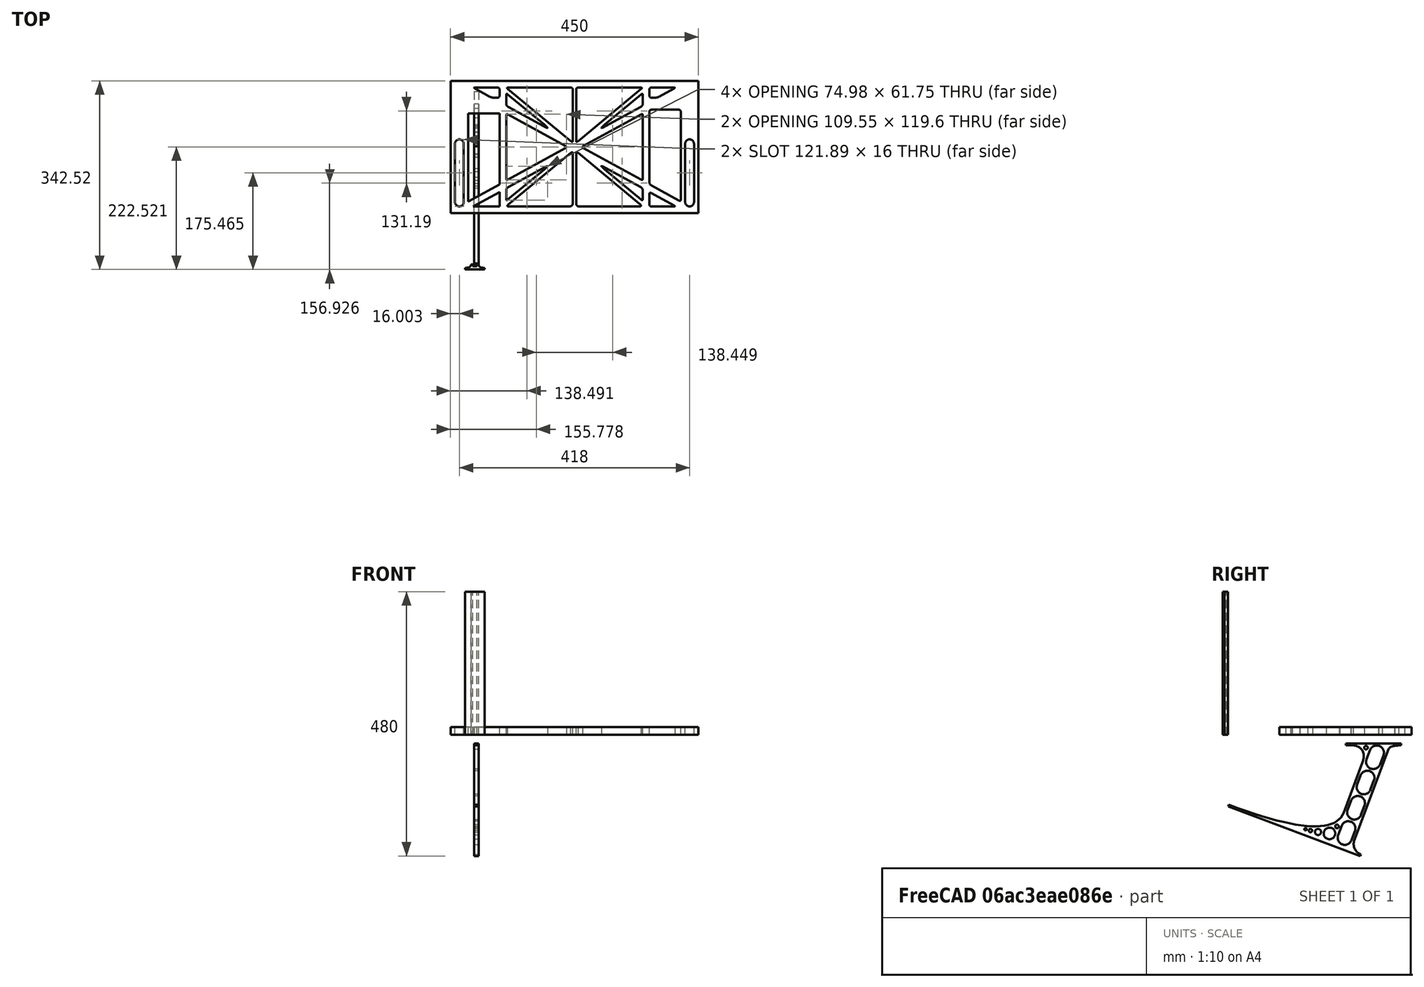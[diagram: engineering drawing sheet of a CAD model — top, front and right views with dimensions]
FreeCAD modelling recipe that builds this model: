
FCSTD DOCUMENT  (FreeCAD 0.19R0.19.2)
Label: laptopStand119FCStd
License: All rights reserved
LicenseURL: http://en.wikipedia.org/wiki/All_rights_reserved
objects: Sketcher::SketchObject×3, Part::Extrusion×3
note: 6 computed .brp shape members not serialized (recipe doc carries the construction recipe); baked Part::Feature solids carry a one-line shape summary decoded from their .brp

FEATURE [Sketcher::SketchObject] Sketch
  FullyConstrained = true
  sketch-geometry (333):
    g0: LineSegment StartX=-10.9272 StartY=-82.7794 StartZ=0 EndX=46.0728 EndY=-51.4823 EndZ=0
    g1: LineSegment StartX=-10.9272 StartY=77.3346 StartZ=0 EndX=-10.9272 EndY=-82.7794 EndZ=0
    g2: LineSegment StartX=-1.92719 StartY=-91.7794 StartZ=0 EndX=46.0728 EndY=-91.7794 EndZ=0
    g3: LineSegment StartX=46.0728 StartY=-65.424 StartZ=0 EndX=-1.92719 EndY=-91.7794 EndZ=0
    g4: LineSegment StartX=46.0728 StartY=-65.424 StartZ=0 EndX=46.0728 EndY=-91.7794 EndZ=0
    g5: LineSegment StartX=46.0728 StartY=77.3346 StartZ=0 EndX=46.0728 EndY=-51.4823 EndZ=0
    g6: LineSegment StartX=-42.9272 StartY=136.221 StartZ=0 EndX=-42.9272 EndY=-103.779 EndZ=0
    g7: LineSegment StartX=407.073 StartY=136.221 StartZ=0 EndX=407.073 EndY=-103.779 EndZ=0
    g8: ArcOfCircle CenterX=-26.9272 CenterY=22.1087 CenterZ=0 NormalX=0 NormalY=0 NormalZ=1 AngleXU=0 Radius=8 StartAngle=1e-16 EndAngle=3.14159
    g9: ArcOfCircle CenterX=-26.9272 CenterY=-83.7794 CenterZ=0 NormalX=0 NormalY=0 NormalZ=1 AngleXU=0 Radius=8 StartAngle=3.14159 EndAngle=6.28319
    g10: LineSegment StartX=-34.9272 StartY=22.1087 StartZ=0 EndX=-34.9272 EndY=-83.7794 EndZ=0
    g11: LineSegment StartX=-18.9272 StartY=22.1087 StartZ=0 EndX=-18.9272 EndY=-83.7794 EndZ=0
    g12: ArcOfCircle CenterX=391.073 CenterY=22.1087 CenterZ=0 NormalX=0 NormalY=0 NormalZ=1 AngleXU=0 Radius=8 StartAngle=-4.4e-15 EndAngle=3.14159
    g13: LineSegment StartX=399.073 StartY=22.1087 StartZ=0 EndX=399.073 EndY=-83.7794 EndZ=0
    g14: LineSegment StartX=383.073 StartY=22.1087 StartZ=0 EndX=383.073 EndY=-83.7794 EndZ=0
    g15: ArcOfCircle CenterX=391.073 CenterY=-83.7794 CenterZ=0 NormalX=0 NormalY=0 NormalZ=1 AngleXU=0 Radius=8 StartAngle=3.14159 EndAngle=6.28319
    g16: Circle CenterX=175.022 CenterY=27.0628 CenterZ=0 NormalX=0 NormalY=0 NormalZ=1 AngleXU=0 Radius=1
    g17: Circle CenterX=179.022 CenterY=24.8665 CenterZ=0 NormalX=0 NormalY=0 NormalZ=1 AngleXU=0 Radius=1
    g18: Circle CenterX=179.022 CenterY=27.0628 CenterZ=0 NormalX=0 NormalY=0 NormalZ=1 AngleXU=0 Radius=1
    g19: BSplineCurve PolesCount=3 KnotsCount=2 Degree=2 IsPeriodic=0
    g20: GeomPoint X=175.022 Y=27.0628 Z=0
    g21: GeomPoint X=179.022 Y=27.0628 Z=0
    g22: Circle CenterX=189.124 CenterY=27.0628 CenterZ=0 NormalX=0 NormalY=0 NormalZ=1 AngleXU=0 Radius=1
    g23: Circle CenterX=185.124 CenterY=24.8665 CenterZ=0 NormalX=0 NormalY=0 NormalZ=1 AngleXU=0 Radius=1
    g24: Circle CenterX=185.124 CenterY=27.0628 CenterZ=0 NormalX=0 NormalY=0 NormalZ=1 AngleXU=0 Radius=1
    g25: BSplineCurve PolesCount=3 KnotsCount=2 Degree=2 IsPeriodic=0
    g26: GeomPoint X=189.124 Y=27.0628 Z=0
    g27: GeomPoint X=185.124 Y=27.0628 Z=0
    g28: Circle CenterX=175.022 CenterY=5.37834 CenterZ=0 NormalX=0 NormalY=0 NormalZ=1 AngleXU=0 Radius=1
    g29: Circle CenterX=179.022 CenterY=7.57463 CenterZ=0 NormalX=0 NormalY=0 NormalZ=1 AngleXU=0 Radius=1
    g30: Circle CenterX=179.022 CenterY=5.34704 CenterZ=0 NormalX=0 NormalY=0 NormalZ=1 AngleXU=0 Radius=1
    g31: BSplineCurve PolesCount=3 KnotsCount=2 Degree=2 IsPeriodic=0
    g32: GeomPoint X=175.022 Y=5.37834 Z=0
    g33: GeomPoint X=179.022 Y=5.34704 Z=0
    g34: Circle CenterX=189.124 CenterY=5.37834 CenterZ=0 NormalX=0 NormalY=0 NormalZ=1 AngleXU=0 Radius=1
    g35: Circle CenterX=185.124 CenterY=7.57463 CenterZ=0 NormalX=0 NormalY=0 NormalZ=1 AngleXU=0 Radius=1
    g36: Circle CenterX=185.124 CenterY=5.34704 CenterZ=0 NormalX=0 NormalY=0 NormalZ=1 AngleXU=0 Radius=1
    g37: BSplineCurve PolesCount=3 KnotsCount=2 Degree=2 IsPeriodic=0
    g38: GeomPoint X=189.124 Y=5.37834 Z=0
    g39: GeomPoint X=185.124 Y=5.34704 Z=0
    g40: Circle CenterX=165.871 CenterY=18.1458 CenterZ=0 NormalX=0 NormalY=0 NormalZ=1 AngleXU=0 Radius=1
    g41: Circle CenterX=169.377 CenterY=16.2206 CenterZ=0 NormalX=0 NormalY=0 NormalZ=1 AngleXU=0 Radius=1
    g42: Circle CenterX=165.871 CenterY=14.2954 CenterZ=0 NormalX=0 NormalY=0 NormalZ=1 AngleXU=0 Radius=1
    g43: BSplineCurve PolesCount=3 KnotsCount=2 Degree=2 IsPeriodic=0
    g44: GeomPoint X=165.871 Y=18.1458 Z=0
    g45: GeomPoint X=165.871 Y=14.2954 Z=0
    g46: Circle CenterX=198.275 CenterY=18.1458 CenterZ=0 NormalX=0 NormalY=0 NormalZ=1 AngleXU=0 Radius=1
    g47: Circle CenterX=194.768 CenterY=16.2206 CenterZ=0 NormalX=0 NormalY=0 NormalZ=1 AngleXU=0 Radius=1
    g48: Circle CenterX=198.275 CenterY=14.2954 CenterZ=0 NormalX=0 NormalY=0 NormalZ=1 AngleXU=0 Radius=1
    g49: BSplineCurve PolesCount=3 KnotsCount=2 Degree=2 IsPeriodic=0
    g50: GeomPoint X=198.275 Y=18.1458 Z=0
    g51: GeomPoint X=198.275 Y=14.2954 Z=0
    g52: LineSegment StartX=407.073 StartY=-103.779 StartZ=0 EndX=-42.9272 EndY=-103.779 EndZ=0
    g53: LineSegment StartX=407.073 StartY=136.221 StartZ=0 EndX=-42.9272 EndY=136.221 EndZ=0
    g54: LineSegment StartX=46.0728 StartY=77.3346 StartZ=0 EndX=-10.9272 EndY=77.3346 EndZ=0
    g55: Circle CenterX=125.607 CenterY=54.1951 CenterZ=0 NormalX=0 NormalY=0 NormalZ=1 AngleXU=0 Radius=1
    g56: Circle CenterX=139.632 CenterY=46.4944 CenterZ=0 NormalX=0 NormalY=0 NormalZ=1 AngleXU=0 Radius=1
    g57: Circle CenterX=127.326 CenterY=56.7187 CenterZ=0 NormalX=0 NormalY=0 NormalZ=1 AngleXU=0 Radius=1
    g58: BSplineCurve PolesCount=3 KnotsCount=2 Degree=2 IsPeriodic=0
    g59: GeomPoint X=125.607 Y=54.1951 Z=0
    g60: GeomPoint X=127.326 Y=56.7187 Z=0
    g61: Circle CenterX=236.821 CenterY=56.7187 CenterZ=0 NormalX=0 NormalY=0 NormalZ=1 AngleXU=0 Radius=1
    g62: Circle CenterX=224.513 CenterY=46.4944 CenterZ=0 NormalX=0 NormalY=0 NormalZ=1 AngleXU=0 Radius=1
    g63: Circle CenterX=238.538 CenterY=54.1951 CenterZ=0 NormalX=0 NormalY=0 NormalZ=1 AngleXU=0 Radius=1
    g64: BSplineCurve PolesCount=3 KnotsCount=2 Degree=2 IsPeriodic=0
    g65: GeomPoint X=236.821 Y=56.7187 Z=0
    g66: GeomPoint X=238.538 Y=54.1951 Z=0
    g67: Circle CenterX=238.538 CenterY=-21.7539 CenterZ=0 NormalX=0 NormalY=0 NormalZ=1 AngleXU=0 Radius=1
    g68: Circle CenterX=224.513 CenterY=-14.0532 CenterZ=0 NormalX=0 NormalY=0 NormalZ=1 AngleXU=0 Radius=1
    g69: Circle CenterX=236.821 CenterY=-24.2775 CenterZ=0 NormalX=0 NormalY=0 NormalZ=1 AngleXU=0 Radius=1
    g70: BSplineCurve PolesCount=3 KnotsCount=2 Degree=2 IsPeriodic=0
    g71: GeomPoint X=238.538 Y=-21.7539 Z=0
    g72: GeomPoint X=236.821 Y=-24.2775 Z=0
    g73: Circle CenterX=125.607 CenterY=-21.7539 CenterZ=0 NormalX=0 NormalY=0 NormalZ=1 AngleXU=0 Radius=1
    g74: Circle CenterX=139.632 CenterY=-14.0532 CenterZ=0 NormalX=0 NormalY=0 NormalZ=1 AngleXU=0 Radius=1
    g75: Circle CenterX=127.325 CenterY=-24.2775 CenterZ=0 NormalX=0 NormalY=0 NormalZ=1 AngleXU=0 Radius=1
    g76: BSplineCurve PolesCount=3 KnotsCount=2 Degree=2 IsPeriodic=0
    g77: GeomPoint X=125.607 Y=-21.7539 Z=0
    g78: GeomPoint X=127.325 Y=-24.2775 Z=0
    g79: Circle CenterX=302.996 CenterY=111.695 CenterZ=0 NormalX=0 NormalY=0 NormalZ=1 AngleXU=0 Radius=1
    g80: Circle CenterX=306.073 CenterY=114.251 CenterZ=0 NormalX=0 NormalY=0 NormalZ=1 AngleXU=0 Radius=1
    g81: Circle CenterX=306.073 CenterY=110.251 CenterZ=0 NormalX=0 NormalY=0 NormalZ=1 AngleXU=0 Radius=1
    g82: BSplineCurve PolesCount=3 KnotsCount=2 Degree=2 IsPeriodic=0
    g83: GeomPoint X=302.996 Y=111.695 Z=0
    g84: GeomPoint X=306.073 Y=110.251 Z=0
    g85: Circle CenterX=306.073 CenterY=95.2763 CenterZ=0 NormalX=0 NormalY=0 NormalZ=1 AngleXU=0 Radius=1
    g86: Circle CenterX=306.073 CenterY=91.2763 CenterZ=0 NormalX=0 NormalY=0 NormalZ=1 AngleXU=0 Radius=1
    g87: Circle CenterX=302.567 CenterY=89.3511 CenterZ=0 NormalX=0 NormalY=0 NormalZ=1 AngleXU=0 Radius=1
    g88: BSplineCurve PolesCount=3 KnotsCount=2 Degree=2 IsPeriodic=0
    g89: GeomPoint X=306.073 Y=95.2763 Z=0
    g90: GeomPoint X=302.567 Y=89.3511 Z=0
    g91: LineSegment StartX=306.073 StartY=110.251 StartZ=0 EndX=306.073 EndY=95.2763 EndZ=0
    g92: LineSegment StartX=302.996 StartY=111.695 StartZ=0 EndX=236.821 EndY=56.7187 EndZ=0
    g93: LineSegment StartX=238.538 StartY=54.1951 StartZ=0 EndX=302.567 EndY=89.3511 EndZ=0
    g94: Circle CenterX=61.1496 CenterY=111.695 CenterZ=0 NormalX=0 NormalY=0 NormalZ=1 AngleXU=0 Radius=1
    g95: Circle CenterX=58.0728 CenterY=114.251 CenterZ=0 NormalX=0 NormalY=0 NormalZ=1 AngleXU=0 Radius=1
    g96: Circle CenterX=58.0728 CenterY=110.251 CenterZ=0 NormalX=0 NormalY=0 NormalZ=1 AngleXU=0 Radius=1
    g97: BSplineCurve PolesCount=3 KnotsCount=2 Degree=2 IsPeriodic=0
    g98: GeomPoint X=61.1496 Y=111.695 Z=0
    g99: GeomPoint X=58.0728 Y=110.251 Z=0
    g100: Circle CenterX=61.5791 CenterY=89.3511 CenterZ=0 NormalX=0 NormalY=0 NormalZ=1 AngleXU=0 Radius=1
    g101: Circle CenterX=58.0728 CenterY=91.2763 CenterZ=0 NormalX=0 NormalY=0 NormalZ=1 AngleXU=0 Radius=1
    g102: Circle CenterX=58.0728 CenterY=95.2763 CenterZ=0 NormalX=0 NormalY=0 NormalZ=1 AngleXU=0 Radius=1
    g103: BSplineCurve PolesCount=3 KnotsCount=2 Degree=2 IsPeriodic=0
    g104: GeomPoint X=61.5791 Y=89.3511 Z=0
    g105: GeomPoint X=58.0728 Y=95.2763 Z=0
    g106: LineSegment StartX=58.0728 StartY=110.251 StartZ=0 EndX=58.0728 EndY=95.2763 EndZ=0
    g107: LineSegment StartX=61.1496 StartY=111.695 StartZ=0 EndX=127.326 EndY=56.7187 EndZ=0
    g108: LineSegment StartX=125.607 StartY=54.1951 StartZ=0 EndX=61.5791 EndY=89.3511 EndZ=0
    g109: Circle CenterX=61.5791 CenterY=-56.9099 CenterZ=0 NormalX=0 NormalY=0 NormalZ=1 AngleXU=0 Radius=1
    g110: Circle CenterX=58.0728 CenterY=-58.8351 CenterZ=0 NormalX=0 NormalY=0 NormalZ=1 AngleXU=0 Radius=1
    g111: Circle CenterX=58.0728 CenterY=-62.8351 CenterZ=0 NormalX=0 NormalY=0 NormalZ=1 AngleXU=0 Radius=1
    g112: BSplineCurve PolesCount=3 KnotsCount=2 Degree=2 IsPeriodic=0
    g113: GeomPoint X=61.5791 Y=-56.9099 Z=0
    g114: GeomPoint X=58.0728 Y=-62.8351 Z=0
    g115: Circle CenterX=58.0728 CenterY=-77.8102 CenterZ=0 NormalX=0 NormalY=0 NormalZ=1 AngleXU=0 Radius=1
    g116: Circle CenterX=58.0728 CenterY=-81.8102 CenterZ=0 NormalX=0 NormalY=0 NormalZ=1 AngleXU=0 Radius=1
    g117: Circle CenterX=61.1496 CenterY=-79.2541 CenterZ=0 NormalX=0 NormalY=0 NormalZ=1 AngleXU=0 Radius=1
    g118: BSplineCurve PolesCount=3 KnotsCount=2 Degree=2 IsPeriodic=0
    g119: GeomPoint X=58.0728 Y=-77.8102 Z=0
    g120: GeomPoint X=61.1496 Y=-79.2541 Z=0
    g121: LineSegment StartX=58.0728 StartY=-62.8351 StartZ=0 EndX=58.0728 EndY=-77.8102 EndZ=0
    g122: LineSegment StartX=61.1496 StartY=-79.2541 StartZ=0 EndX=127.325 EndY=-24.2775 EndZ=0
    g123: LineSegment StartX=125.607 StartY=-21.7539 StartZ=0 EndX=61.5791 EndY=-56.9099 EndZ=0
    g124: Circle CenterX=302.567 CenterY=-56.9099 CenterZ=0 NormalX=0 NormalY=0 NormalZ=1 AngleXU=0 Radius=1
    g125: Circle CenterX=306.073 CenterY=-58.8351 CenterZ=0 NormalX=0 NormalY=0 NormalZ=1 AngleXU=0 Radius=1
    g126: Circle CenterX=306.073 CenterY=-62.8351 CenterZ=0 NormalX=0 NormalY=0 NormalZ=1 AngleXU=0 Radius=1
    g127: BSplineCurve PolesCount=3 KnotsCount=2 Degree=2 IsPeriodic=0
    g128: GeomPoint X=302.567 Y=-56.9099 Z=0
    g129: GeomPoint X=306.073 Y=-62.8351 Z=0
    g130: Circle CenterX=302.996 CenterY=-79.2541 CenterZ=0 NormalX=0 NormalY=0 NormalZ=1 AngleXU=0 Radius=1
    g131: Circle CenterX=306.073 CenterY=-81.8102 CenterZ=0 NormalX=0 NormalY=0 NormalZ=1 AngleXU=0 Radius=1
    g132: Circle CenterX=306.073 CenterY=-77.8102 CenterZ=0 NormalX=0 NormalY=0 NormalZ=1 AngleXU=0 Radius=1
    g133: BSplineCurve PolesCount=3 KnotsCount=2 Degree=2 IsPeriodic=0
    g134: GeomPoint X=302.996 Y=-79.2541 Z=0
    g135: GeomPoint X=306.073 Y=-77.8102 Z=0
    g136: LineSegment StartX=306.073 StartY=-62.8351 StartZ=0 EndX=306.073 EndY=-77.8102 EndZ=0
    g137: LineSegment StartX=302.996 StartY=-79.2541 StartZ=0 EndX=236.821 EndY=-24.2775 EndZ=0
    g138: LineSegment StartX=238.538 StartY=-21.7539 StartZ=0 EndX=302.567 EndY=-56.9099 EndZ=0
    g139: Circle CenterX=61.6457 CenterY=-88.8112 CenterZ=0 NormalX=0 NormalY=0 NormalZ=1 AngleXU=0 Radius=1
    g140: Circle CenterX=58.0728 CenterY=-91.7794 CenterZ=0 NormalX=0 NormalY=0 NormalZ=1 AngleXU=0 Radius=1
    g141: Circle CenterX=63.9135 CenterY=-91.7794 CenterZ=0 NormalX=0 NormalY=0 NormalZ=1 AngleXU=0 Radius=1
    g142: BSplineCurve PolesCount=3 KnotsCount=2 Degree=2 IsPeriodic=0
    g143: GeomPoint X=61.6457 Y=-88.8112 Z=0
    g144: GeomPoint X=63.9135 Y=-91.7794 Z=0
    g145: Circle CenterX=179.022 CenterY=-85.8163 CenterZ=0 NormalX=0 NormalY=0 NormalZ=1 AngleXU=0 Radius=1
    g146: Circle CenterX=179.022 CenterY=-91.7794 CenterZ=0 NormalX=0 NormalY=0 NormalZ=1 AngleXU=0 Radius=1
    g147: Circle CenterX=171.895 CenterY=-91.7794 CenterZ=0 NormalX=0 NormalY=0 NormalZ=1 AngleXU=0 Radius=1
    g148: BSplineCurve PolesCount=3 KnotsCount=2 Degree=2 IsPeriodic=0
    g149: GeomPoint X=179.022 Y=-85.8163 Z=0
    g150: GeomPoint X=171.895 Y=-91.7794 Z=0
    g151: Circle CenterX=185.124 CenterY=-86.2028 CenterZ=0 NormalX=0 NormalY=0 NormalZ=1 AngleXU=0 Radius=1
    g152: Circle CenterX=185.124 CenterY=-91.7794 CenterZ=0 NormalX=0 NormalY=0 NormalZ=1 AngleXU=0 Radius=1
    g153: Circle CenterX=191.747 CenterY=-91.7794 CenterZ=0 NormalX=0 NormalY=0 NormalZ=1 AngleXU=0 Radius=1
    g154: BSplineCurve PolesCount=3 KnotsCount=2 Degree=2 IsPeriodic=0
    g155: GeomPoint X=185.124 Y=-86.2028 Z=0
    g156: GeomPoint X=191.747 Y=-91.7794 Z=0
    g157: Circle CenterX=299.888 CenterY=-86.6413 CenterZ=0 NormalX=0 NormalY=0 NormalZ=1 AngleXU=0 Radius=1
    g158: Circle CenterX=306.073 CenterY=-91.7794 CenterZ=0 NormalX=0 NormalY=0 NormalZ=1 AngleXU=0 Radius=1
    g159: Circle CenterX=298.776 CenterY=-91.7794 CenterZ=0 NormalX=0 NormalY=0 NormalZ=1 AngleXU=0 Radius=1
    g160: BSplineCurve PolesCount=3 KnotsCount=2 Degree=2 IsPeriodic=0
    g161: GeomPoint X=299.888 Y=-86.6413 Z=0
    g162: GeomPoint X=298.776 Y=-91.7794 Z=0
    g163: LineSegment StartX=189.124 StartY=5.37834 StartZ=0 EndX=299.888 EndY=-86.6413 EndZ=0
    g164: LineSegment StartX=298.776 StartY=-91.7794 StartZ=0 EndX=191.747 EndY=-91.7794 EndZ=0
    g165: LineSegment StartX=185.124 StartY=-86.2028 StartZ=0 EndX=185.124 EndY=5.34704 EndZ=0
    g166: LineSegment StartX=179.022 StartY=5.34704 StartZ=0 EndX=179.022 EndY=-85.8163 EndZ=0
    g167: LineSegment StartX=171.895 StartY=-91.7794 StartZ=0 EndX=63.9135 EndY=-91.7794 EndZ=0
    g168: LineSegment StartX=61.6457 StartY=-88.8112 StartZ=0 EndX=175.022 EndY=5.37834 EndZ=0
    g169: Circle CenterX=302.073 CenterY=124.221 CenterZ=0 NormalX=0 NormalY=0 NormalZ=1 AngleXU=0 Radius=1
    g170: Circle CenterX=306.073 CenterY=124.221 CenterZ=0 NormalX=0 NormalY=0 NormalZ=1 AngleXU=0 Radius=1
    g171: Circle CenterX=302.996 CenterY=121.665 CenterZ=0 NormalX=0 NormalY=0 NormalZ=1 AngleXU=0 Radius=1
    g172: BSplineCurve PolesCount=3 KnotsCount=2 Degree=2 IsPeriodic=0
    g173: GeomPoint X=302.073 Y=124.221 Z=0
    g174: GeomPoint X=302.996 Y=121.665 Z=0
    g175: Circle CenterX=189.124 CenterY=124.221 CenterZ=0 NormalX=0 NormalY=0 NormalZ=1 AngleXU=0 Radius=1
    g176: Circle CenterX=185.124 CenterY=124.221 CenterZ=0 NormalX=0 NormalY=0 NormalZ=1 AngleXU=0 Radius=1
    g177: Circle CenterX=185.124 CenterY=120.221 CenterZ=0 NormalX=0 NormalY=0 NormalZ=1 AngleXU=0 Radius=1
    g178: BSplineCurve PolesCount=3 KnotsCount=2 Degree=2 IsPeriodic=0
    g179: GeomPoint X=189.124 Y=124.221 Z=0
    g180: GeomPoint X=185.124 Y=120.221 Z=0
    g181: Circle CenterX=175.022 CenterY=124.221 CenterZ=0 NormalX=0 NormalY=0 NormalZ=1 AngleXU=0 Radius=1
    g182: Circle CenterX=179.022 CenterY=124.221 CenterZ=0 NormalX=0 NormalY=0 NormalZ=1 AngleXU=0 Radius=1
    g183: Circle CenterX=179.022 CenterY=120.221 CenterZ=0 NormalX=0 NormalY=0 NormalZ=1 AngleXU=0 Radius=1
    g184: BSplineCurve PolesCount=3 KnotsCount=2 Degree=2 IsPeriodic=0
    g185: GeomPoint X=175.022 Y=124.221 Z=0
    g186: GeomPoint X=179.022 Y=120.221 Z=0
    g187: Circle CenterX=62.0728 CenterY=124.221 CenterZ=0 NormalX=0 NormalY=0 NormalZ=1 AngleXU=0 Radius=1
    g188: Circle CenterX=58.0728 CenterY=124.221 CenterZ=0 NormalX=0 NormalY=0 NormalZ=1 AngleXU=0 Radius=1
    g189: Circle CenterX=61.1496 CenterY=121.665 CenterZ=0 NormalX=0 NormalY=0 NormalZ=1 AngleXU=0 Radius=1
    g190: BSplineCurve PolesCount=3 KnotsCount=2 Degree=2 IsPeriodic=0
    g191: GeomPoint X=62.0728 Y=124.221 Z=0
    g192: GeomPoint X=61.1496 Y=121.665 Z=0
    g193: LineSegment StartX=62.0728 StartY=124.221 StartZ=0 EndX=175.022 EndY=124.221 EndZ=0
    g194: LineSegment StartX=179.022 StartY=120.221 StartZ=0 EndX=179.022 EndY=27.0628 EndZ=0
    g195: LineSegment StartX=185.124 StartY=27.0628 StartZ=0 EndX=185.124 EndY=120.221 EndZ=0
    g196: LineSegment StartX=189.124 StartY=124.221 StartZ=0 EndX=302.073 EndY=124.221 EndZ=0
    g197: LineSegment StartX=302.996 StartY=121.665 StartZ=0 EndX=189.124 EndY=27.0628 EndZ=0
    g198: LineSegment StartX=175.022 StartY=27.0628 StartZ=0 EndX=61.1496 EndY=121.665 EndZ=0
    g199: Circle CenterX=61.5791 CenterY=75.4095 CenterZ=0 NormalX=0 NormalY=0 NormalZ=1 AngleXU=0 Radius=1
    g200: Circle CenterX=58.0728 CenterY=77.3346 CenterZ=0 NormalX=0 NormalY=0 NormalZ=1 AngleXU=0 Radius=1
    g201: Circle CenterX=58.0728 CenterY=73.3346 CenterZ=0 NormalX=0 NormalY=0 NormalZ=1 AngleXU=0 Radius=1
    g202: BSplineCurve PolesCount=3 KnotsCount=2 Degree=2 IsPeriodic=0
    g203: GeomPoint X=61.5791 Y=75.4095 Z=0
    g204: GeomPoint X=58.0728 Y=73.3346 Z=0
    g205: Circle CenterX=58.0728 CenterY=-40.8935 CenterZ=0 NormalX=0 NormalY=0 NormalZ=1 AngleXU=0 Radius=1
    g206: Circle CenterX=58.0728 CenterY=-44.8935 CenterZ=0 NormalX=0 NormalY=0 NormalZ=1 AngleXU=0 Radius=1
    g207: Circle CenterX=61.5791 CenterY=-42.9683 CenterZ=0 NormalX=0 NormalY=0 NormalZ=1 AngleXU=0 Radius=1
    g208: BSplineCurve PolesCount=3 KnotsCount=2 Degree=2 IsPeriodic=0
    g209: GeomPoint X=58.0728 Y=-40.8935 Z=0
    g210: GeomPoint X=61.5791 Y=-42.9683 Z=0
    g211: LineSegment StartX=61.5791 StartY=-42.9683 StartZ=0 EndX=165.871 EndY=14.2954 EndZ=0
    g212: LineSegment StartX=165.871 StartY=18.1458 StartZ=0 EndX=61.5791 EndY=75.4095 EndZ=0
    g213: LineSegment StartX=58.0728 StartY=73.3346 StartZ=0 EndX=58.0728 EndY=-40.8935 EndZ=0
    g214: Circle CenterX=302.567 CenterY=-42.9683 CenterZ=0 NormalX=0 NormalY=0 NormalZ=1 AngleXU=0 Radius=1
    g215: Circle CenterX=306.073 CenterY=-44.8935 CenterZ=0 NormalX=0 NormalY=0 NormalZ=1 AngleXU=0 Radius=1
    g216: Circle CenterX=306.073 CenterY=-40.8935 CenterZ=0 NormalX=0 NormalY=0 NormalZ=1 AngleXU=0 Radius=1
    g217: BSplineCurve PolesCount=3 KnotsCount=2 Degree=2 IsPeriodic=0
    g218: GeomPoint X=302.567 Y=-42.9683 Z=0
    g219: GeomPoint X=306.073 Y=-40.8935 Z=0
    g220: Circle CenterX=306.073 CenterY=73.3346 CenterZ=0 NormalX=0 NormalY=0 NormalZ=1 AngleXU=0 Radius=1
    g221: Circle CenterX=306.073 CenterY=77.3346 CenterZ=0 NormalX=0 NormalY=0 NormalZ=1 AngleXU=0 Radius=1
    g222: Circle CenterX=302.567 CenterY=75.4095 CenterZ=0 NormalX=0 NormalY=0 NormalZ=1 AngleXU=0 Radius=1
    g223: BSplineCurve PolesCount=3 KnotsCount=2 Degree=2 IsPeriodic=0
    g224: GeomPoint X=306.073 Y=73.3346 Z=0
    g225: GeomPoint X=302.567 Y=75.4095 Z=0
    g226: LineSegment StartX=302.567 StartY=-42.9683 StartZ=0 EndX=198.275 EndY=14.2954 EndZ=0
    g227: LineSegment StartX=198.275 StartY=18.1458 StartZ=0 EndX=302.567 EndY=75.4095 EndZ=0
    g228: LineSegment StartX=306.073 StartY=73.3346 StartZ=0 EndX=306.073 EndY=-40.8935 EndZ=0
    g229: LineSegment StartX=322.073 StartY=105.865 StartZ=0 EndX=328.643 EndY=105.865 EndZ=0
    g230: LineSegment StartX=318.073 StartY=120.221 StartZ=0 EndX=318.073 EndY=109.865 EndZ=0
    g231: LineSegment StartX=336.157 StartY=107.779 StartZ=0 EndX=362.567 EndY=122.294 EndZ=0
    g232: Circle CenterX=362.073 CenterY=124.221 CenterZ=0 NormalX=0 NormalY=0 NormalZ=1 AngleXU=0 Radius=1
    g233: Circle CenterX=366.073 CenterY=124.221 CenterZ=0 NormalX=0 NormalY=0 NormalZ=1 AngleXU=0 Radius=1
    g234: Circle CenterX=362.567 CenterY=122.294 CenterZ=0 NormalX=0 NormalY=0 NormalZ=1 AngleXU=0 Radius=1
    g235: BSplineCurve PolesCount=3 KnotsCount=2 Degree=2 IsPeriodic=0
    g236: GeomPoint X=362.073 Y=124.221 Z=0
    g237: GeomPoint X=362.567 Y=122.294 Z=0
    g238: Circle CenterX=322.073 CenterY=124.221 CenterZ=0 NormalX=0 NormalY=0 NormalZ=1 AngleXU=0 Radius=1
    g239: Circle CenterX=318.073 CenterY=124.221 CenterZ=0 NormalX=0 NormalY=0 NormalZ=1 AngleXU=0 Radius=1
    g240: Circle CenterX=318.073 CenterY=120.221 CenterZ=0 NormalX=0 NormalY=0 NormalZ=1 AngleXU=0 Radius=1
    g241: BSplineCurve PolesCount=3 KnotsCount=2 Degree=2 IsPeriodic=0
    g242: GeomPoint X=322.073 Y=124.221 Z=0
    g243: GeomPoint X=318.073 Y=120.221 Z=0
    g244: Circle CenterX=322.073 CenterY=105.865 CenterZ=0 NormalX=0 NormalY=0 NormalZ=1 AngleXU=0 Radius=1
    g245: Circle CenterX=318.073 CenterY=105.865 CenterZ=0 NormalX=0 NormalY=0 NormalZ=1 AngleXU=0 Radius=1
    g246: Circle CenterX=318.073 CenterY=109.865 CenterZ=0 NormalX=0 NormalY=0 NormalZ=1 AngleXU=0 Radius=1
    g247: BSplineCurve PolesCount=3 KnotsCount=2 Degree=2 IsPeriodic=0
    g248: GeomPoint X=322.073 Y=105.865 Z=0
    g249: GeomPoint X=318.073 Y=109.865 Z=0
    g250: Circle CenterX=336.157 CenterY=107.779 CenterZ=0 NormalX=0 NormalY=0 NormalZ=1 AngleXU=0 Radius=1
    g251: Circle CenterX=332.651 CenterY=105.853 CenterZ=0 NormalX=0 NormalY=0 NormalZ=1 AngleXU=0 Radius=1
    g252: Circle CenterX=328.643 CenterY=105.865 CenterZ=0 NormalX=0 NormalY=0 NormalZ=1 AngleXU=0 Radius=1
    g253: BSplineCurve PolesCount=3 KnotsCount=2 Degree=2 IsPeriodic=0
    g254: GeomPoint X=336.157 Y=107.779 Z=0
    g255: GeomPoint X=328.643 Y=105.865 Z=0
    g256: LineSegment StartX=322.073 StartY=124.221 StartZ=0 EndX=362.073 EndY=124.221 EndZ=0
    g257: Circle CenterX=371.567 CenterY=-80.8644 CenterZ=0 NormalX=0 NormalY=0 NormalZ=1 AngleXU=0 Radius=1
    g258: Circle CenterX=375.073 CenterY=-82.7896 CenterZ=0 NormalX=0 NormalY=0 NormalZ=1 AngleXU=0 Radius=1
    g259: Circle CenterX=375.073 CenterY=-78.7896 CenterZ=0 NormalX=0 NormalY=0 NormalZ=1 AngleXU=0 Radius=1
    g260: BSplineCurve PolesCount=3 KnotsCount=2 Degree=2 IsPeriodic=0
    g261: GeomPoint X=371.567 Y=-80.8644 Z=0
    g262: GeomPoint X=375.073 Y=-78.7896 Z=0
    g263: Circle CenterX=321.579 CenterY=-53.4075 CenterZ=0 NormalX=0 NormalY=0 NormalZ=1 AngleXU=0 Radius=1
    g264: Circle CenterX=318.073 CenterY=-51.4823 CenterZ=0 NormalX=0 NormalY=0 NormalZ=1 AngleXU=0 Radius=1
    g265: Circle CenterX=318.073 CenterY=-47.4823 CenterZ=0 NormalX=0 NormalY=0 NormalZ=1 AngleXU=0 Radius=1
    g266: BSplineCurve PolesCount=3 KnotsCount=2 Degree=2 IsPeriodic=0
    g267: GeomPoint X=321.579 Y=-53.4075 Z=0
    g268: GeomPoint X=318.073 Y=-47.4823 Z=0
    g269: Circle CenterX=318.073 CenterY=79.9235 CenterZ=0 NormalX=0 NormalY=0 NormalZ=1 AngleXU=0 Radius=1
    g270: Circle CenterX=318.073 CenterY=83.9235 CenterZ=0 NormalX=0 NormalY=0 NormalZ=1 AngleXU=0 Radius=1
    g271: Circle CenterX=322.073 CenterY=83.9235 CenterZ=0 NormalX=0 NormalY=0 NormalZ=1 AngleXU=0 Radius=1
    g272: BSplineCurve PolesCount=3 KnotsCount=2 Degree=2 IsPeriodic=0
    g273: GeomPoint X=318.073 Y=79.9235 Z=0
    g274: GeomPoint X=322.073 Y=83.9235 Z=0
    g275: Circle CenterX=375.073 CenterY=79.9235 CenterZ=0 NormalX=0 NormalY=0 NormalZ=1 AngleXU=0 Radius=1
    g276: Circle CenterX=375.073 CenterY=83.9235 CenterZ=0 NormalX=0 NormalY=0 NormalZ=1 AngleXU=0 Radius=1
    g277: Circle CenterX=371.073 CenterY=83.9235 CenterZ=0 NormalX=0 NormalY=0 NormalZ=1 AngleXU=0 Radius=1
    g278: BSplineCurve PolesCount=3 KnotsCount=2 Degree=2 IsPeriodic=0
    g279: GeomPoint X=375.073 Y=79.9235 Z=0
    g280: GeomPoint X=371.073 Y=83.9235 Z=0
    g281: LineSegment StartX=322.073 StartY=83.9235 StartZ=0 EndX=371.073 EndY=83.9235 EndZ=0
    g282: LineSegment StartX=375.073 StartY=79.9235 StartZ=0 EndX=375.073 EndY=-78.7896 EndZ=0
    g283: LineSegment StartX=371.567 StartY=-80.8644 StartZ=0 EndX=321.579 EndY=-53.4075 EndZ=0
    g284: LineSegment StartX=318.073 StartY=-47.4823 StartZ=0 EndX=318.073 EndY=79.9235 EndZ=0
    g285: Circle CenterX=321.579 CenterY=-67.3492 CenterZ=0 NormalX=0 NormalY=0 NormalZ=1 AngleXU=0 Radius=1
    g286: Circle CenterX=318.073 CenterY=-65.424 CenterZ=0 NormalX=0 NormalY=0 NormalZ=1 AngleXU=0 Radius=1
    g287: Circle CenterX=318.073 CenterY=-69.424 CenterZ=0 NormalX=0 NormalY=0 NormalZ=1 AngleXU=0 Radius=1
    g288: BSplineCurve PolesCount=3 KnotsCount=2 Degree=2 IsPeriodic=0
    g289: GeomPoint X=321.579 Y=-67.3492 Z=0
    g290: GeomPoint X=318.073 Y=-69.424 Z=0
    g291: Circle CenterX=362.567 CenterY=-89.8542 CenterZ=0 NormalX=0 NormalY=0 NormalZ=1 AngleXU=0 Radius=1
    g292: Circle CenterX=366.073 CenterY=-91.7794 CenterZ=0 NormalX=0 NormalY=0 NormalZ=1 AngleXU=0 Radius=1
    g293: Circle CenterX=362.073 CenterY=-91.7794 CenterZ=0 NormalX=0 NormalY=0 NormalZ=1 AngleXU=0 Radius=1
    g294: BSplineCurve PolesCount=3 KnotsCount=2 Degree=2 IsPeriodic=0
    g295: GeomPoint X=362.567 Y=-89.8542 Z=0
    g296: GeomPoint X=362.073 Y=-91.7794 Z=0
    g297: Circle CenterX=322.073 CenterY=-91.7794 CenterZ=0 NormalX=0 NormalY=0 NormalZ=1 AngleXU=0 Radius=1
    g298: Circle CenterX=318.073 CenterY=-91.7794 CenterZ=0 NormalX=0 NormalY=0 NormalZ=1 AngleXU=0 Radius=1
    g299: Circle CenterX=318.073 CenterY=-87.7794 CenterZ=0 NormalX=0 NormalY=0 NormalZ=1 AngleXU=0 Radius=1
    g300: BSplineCurve PolesCount=3 KnotsCount=2 Degree=2 IsPeriodic=0
    g301: GeomPoint X=322.073 Y=-91.7794 Z=0
    g302: GeomPoint X=318.073 Y=-87.7794 Z=0
    g303: LineSegment StartX=362.567 StartY=-89.8542 StartZ=0 EndX=321.579 EndY=-67.3492 EndZ=0
    g304: LineSegment StartX=318.073 StartY=-69.424 StartZ=0 EndX=318.073 EndY=-87.7794 EndZ=0
    g305: LineSegment StartX=322.073 StartY=-91.7794 StartZ=0 EndX=362.073 EndY=-91.7794 EndZ=0
    g306: Circle CenterX=2.07281 CenterY=124.221 CenterZ=0 NormalX=0 NormalY=0 NormalZ=1 AngleXU=0 Radius=1
    g307: Circle CenterX=1.57905 CenterY=122.295 CenterZ=0 NormalX=0 NormalY=0 NormalZ=1 AngleXU=0 Radius=1
    g308: BSplineCurve PolesCount=3 KnotsCount=2 Degree=2 IsPeriodic=0
    g309: GeomPoint X=2.07281 Y=124.221 Z=0
    g310: GeomPoint X=1.57905 Y=122.295 Z=0
    g311: Circle CenterX=42.0728 CenterY=124.221 CenterZ=0 NormalX=0 NormalY=0 NormalZ=1 AngleXU=0 Radius=1
    g312: Circle CenterX=46.0728 CenterY=124.221 CenterZ=0 NormalX=0 NormalY=0 NormalZ=1 AngleXU=0 Radius=1
    g313: Circle CenterX=46.0728 CenterY=120.221 CenterZ=0 NormalX=0 NormalY=0 NormalZ=1 AngleXU=0 Radius=1
    g314: BSplineCurve PolesCount=3 KnotsCount=2 Degree=2 IsPeriodic=0
    g315: GeomPoint X=42.0728 Y=124.221 Z=0
    g316: GeomPoint X=46.0728 Y=120.221 Z=0
    g317: Circle CenterX=46.0728 CenterY=109.865 CenterZ=0 NormalX=0 NormalY=0 NormalZ=1 AngleXU=0 Radius=1
    g318: Circle CenterX=46.0728 CenterY=105.865 CenterZ=0 NormalX=0 NormalY=0 NormalZ=1 AngleXU=0 Radius=1
    g319: Circle CenterX=42.0728 CenterY=105.865 CenterZ=0 NormalX=0 NormalY=0 NormalZ=1 AngleXU=0 Radius=1
    g320: BSplineCurve PolesCount=3 KnotsCount=2 Degree=2 IsPeriodic=0
    g321: GeomPoint X=46.0728 Y=109.865 Z=0
    g322: GeomPoint X=42.0728 Y=105.865 Z=0
    g323: Circle CenterX=35.5028 CenterY=105.865 CenterZ=0 NormalX=0 NormalY=0 NormalZ=1 AngleXU=0 Radius=1
    g324: Circle CenterX=31.5028 CenterY=105.865 CenterZ=0 NormalX=0 NormalY=0 NormalZ=1 AngleXU=0 Radius=1
    g325: Circle CenterX=27.9965 CenterY=107.79 CenterZ=0 NormalX=0 NormalY=0 NormalZ=1 AngleXU=0 Radius=1
    g326: BSplineCurve PolesCount=3 KnotsCount=2 Degree=2 IsPeriodic=0
    g327: GeomPoint X=35.5028 Y=105.865 Z=0
    g328: GeomPoint X=27.9965 Y=107.79 Z=0
    g329: LineSegment StartX=2.07281 StartY=124.221 StartZ=0 EndX=42.0728 EndY=124.221 EndZ=0
    g330: LineSegment StartX=46.0728 StartY=120.221 StartZ=0 EndX=46.0728 EndY=109.865 EndZ=0
    g331: LineSegment StartX=42.0728 StartY=105.865 StartZ=0 EndX=35.5028 EndY=105.865 EndZ=0
    g332: LineSegment StartX=27.9965 StartY=107.79 StartZ=0 EndX=1.57905 EndY=122.295 EndZ=0
  constraints (552):
    c: Horizontal(g2)
    c: Coincident(g4,g3)
    c: Coincident(g0,g5)
    c: Block(g4)
    c: Block(g3)
    c: Block(g0)
    c: Block(g1)
    c: Block(g2)
    c: Vertical(g6)
    c: Vertical(g7)
    c: Block(g7)
    c: Block(g6)
    c: Tangent(g8,g11) = 1.5708
    c: Tangent(g8,g10) = -1.5708
    c: Tangent(g10,g9) = -1.5708
    c: Tangent(g11,g9) = 1.5708
    c: Vertical(g10)
    c: Equal(g8,g9)
    c: Block(g11)
    c: Block(g10)
    c: Tangent(g12,g13) = 1.5708
    c: Tangent(g13,g15) = 1.5708
    c: Equal(g12,g15)
    c: Coincident(g14,g12)
    c: Coincident(g14,g15)
    c: Block(g13)
    c: Block(g14)
    c: Weight(g16) = 1
    c: Equal(g16,g17)
    c: Equal(g16,g18)
    c: InternalAlignment(g16,g19)
    c: InternalAlignment(g17,g19)
    c: InternalAlignment(g18,g19)
    c: InternalAlignment(g20,g19)
    c: InternalAlignment(g21,g19)
    c: Weight(g22) = 1
    c: Equal(g22,g23)
    c: Equal(g22,g24)
    c: InternalAlignment(g22,g25)
    c: InternalAlignment(g23,g25)
    c: InternalAlignment(g24,g25)
    c: InternalAlignment(g26,g25)
    c: InternalAlignment(g27,g25)
    c: Block(g25)
    c: Block(g19)
    c: Weight(g28) = 1
    c: Equal(g28,g29)
    c: Equal(g28,g30)
    c: InternalAlignment(g28,g31)
    c: InternalAlignment(g29,g31)
    c: InternalAlignment(g30,g31)
    c: InternalAlignment(g32,g31)
    c: InternalAlignment(g33,g31)
    c: Weight(g34) = 1
    c: Equal(g34,g35)
    c: Equal(g34,g36)
    c: InternalAlignment(g34,g37)
    c: InternalAlignment(g35,g37)
    c: InternalAlignment(g36,g37)
    c: InternalAlignment(g38,g37)
    c: InternalAlignment(g39,g37)
    c: Block(g37)
    c: Block(g31)
    c: Weight(g40) = 1
    c: Equal(g40,g41)
    c: Equal(g40,g42)
    c: InternalAlignment(g40,g43)
    c: InternalAlignment(g41,g43)
    c: InternalAlignment(g42,g43)
    c: InternalAlignment(g44,g43)
    c: InternalAlignment(g45,g43)
    c: Weight(g46) = 1
    c: Equal(g46,g47)
    c: Equal(g46,g48)
    c: InternalAlignment(g46,g49)
    c: InternalAlignment(g47,g49)
    c: InternalAlignment(g48,g49)
    c: InternalAlignment(g50,g49)
    c: InternalAlignment(g51,g49)
    c: Block(g43)
    c: Block(g49)
    c: Coincident(g52,g7)
    c: Coincident(g52,g6)
    c: Horizontal(g52)
    c: Distance(g52) = 450
    c: Coincident(g53,g7)
    c: Coincident(g53,g6)
    c: Horizontal(g53)
    c: Horizontal(g54)
    c: Coincident(g5,g54)
    c: Block(g54)
    c: Coincident(g1,g54)
    c: Weight(g55) = 1
    c: Equal(g55,g56)
    c: Equal(g55,g57)
    c: InternalAlignment(g55,g58)
    c: InternalAlignment(g56,g58)
    c: InternalAlignment(g57,g58)
    c: InternalAlignment(g59,g58)
    c: InternalAlignment(g60,g58)
    c: Block(g58)
    c: Weight(g61) = 1
    c: Equal(g61,g62)
    c: Equal(g61,g63)
    c: InternalAlignment(g61,g64)
    c: InternalAlignment(g62,g64)
    c: InternalAlignment(g63,g64)
    c: InternalAlignment(g65,g64)
    c: InternalAlignment(g66,g64)
    c: Block(g64)
    c: Weight(g67) = 1
    c: Equal(g67,g68)
    c: Equal(g67,g69)
    c: InternalAlignment(g67,g70)
    c: InternalAlignment(g68,g70)
    c: InternalAlignment(g69,g70)
    c: InternalAlignment(g71,g70)
    c: InternalAlignment(g72,g70)
    c: Block(g70)
    c: Weight(g73) = 1
    c: Equal(g73,g74)
    c: Equal(g73,g75)
    c: InternalAlignment(g73,g76)
    c: InternalAlignment(g74,g76)
    c: InternalAlignment(g75,g76)
    c: InternalAlignment(g77,g76)
    c: InternalAlignment(g78,g76)
    c: Block(g76)
    c: Weight(g79) = 1
    c: Equal(g79,g80)
    c: Equal(g79,g81)
    c: InternalAlignment(g79,g82)
    c: InternalAlignment(g80,g82)
    c: InternalAlignment(g81,g82)
    c: InternalAlignment(g83,g82)
    c: InternalAlignment(g84,g82)
    c: Weight(g85) = 1
    c: Equal(g85,g86)
    c: Equal(g85,g87)
    c: InternalAlignment(g85,g88)
    c: InternalAlignment(g86,g88)
    c: InternalAlignment(g87,g88)
    c: InternalAlignment(g89,g88)
    c: InternalAlignment(g90,g88)
    c: Block(g82)
    c: Block(g88)
    c: Coincident(g91,g82)
    c: Coincident(g91,g88)
    c: Vertical(g91)
    c: Coincident(g92,g82)
    c: Coincident(g92,g64)
    c: Coincident(g93,g64)
    c: Coincident(g93,g88)
    c: Weight(g94) = 1
    c: Equal(g94,g95)
    c: Equal(g94,g96)
    c: InternalAlignment(g94,g97)
    c: InternalAlignment(g95,g97)
    c: InternalAlignment(g96,g97)
    c: InternalAlignment(g98,g97)
    c: InternalAlignment(g99,g97)
    c: Weight(g100) = 1
    c: Equal(g100,g101)
    c: Equal(g100,g102)
    c: InternalAlignment(g100,g103)
    c: InternalAlignment(g101,g103)
    c: InternalAlignment(g102,g103)
    c: InternalAlignment(g104,g103)
    c: InternalAlignment(g105,g103)
    c: Block(g97)
    c: Block(g103)
    c: Coincident(g106,g97)
    c: Coincident(g106,g103)
    c: Vertical(g106)
    c: Coincident(g107,g97)
    c: Coincident(g107,g58)
    c: Coincident(g108,g58)
    c: Coincident(g108,g103)
    c: Weight(g109) = 1
    c: Equal(g109,g110)
    c: Equal(g109,g111)
    c: InternalAlignment(g109,g112)
    c: InternalAlignment(g110,g112)
    c: InternalAlignment(g111,g112)
    c: InternalAlignment(g113,g112)
    c: InternalAlignment(g114,g112)
    c: Weight(g115) = 1
    c: Equal(g115,g116)
    c: Equal(g115,g117)
    c: InternalAlignment(g115,g118)
    c: InternalAlignment(g116,g118)
    c: InternalAlignment(g117,g118)
    c: InternalAlignment(g119,g118)
    c: InternalAlignment(g120,g118)
    c: Block(g112)
    c: Block(g118)
    c: Coincident(g121,g112)
    c: Coincident(g121,g118)
    c: Vertical(g121)
    c: Coincident(g122,g118)
    c: Coincident(g122,g76)
    c: Coincident(g123,g76)
    c: Coincident(g123,g112)
    c: Weight(g124) = 1
    c: Equal(g124,g125)
    c: Equal(g124,g126)
    c: InternalAlignment(g124,g127)
    c: InternalAlignment(g125,g127)
    c: InternalAlignment(g126,g127)
    c: InternalAlignment(g128,g127)
    c: InternalAlignment(g129,g127)
    c: Weight(g130) = 1
    c: Equal(g130,g131)
    c: Equal(g130,g132)
    c: InternalAlignment(g130,g133)
    c: InternalAlignment(g131,g133)
    c: InternalAlignment(g132,g133)
    c: InternalAlignment(g134,g133)
    c: InternalAlignment(g135,g133)
    c: Block(g127)
    c: Block(g133)
    c: Coincident(g136,g127)
    c: Coincident(g136,g133)
    c: Vertical(g136)
    c: Coincident(g137,g133)
    c: Coincident(g137,g70)
    c: Coincident(g138,g70)
    c: Coincident(g138,g127)
    c: Weight(g139) = 1
    c: Equal(g139,g140)
    c: Equal(g139,g141)
    c: InternalAlignment(g139,g142)
    c: InternalAlignment(g140,g142)
    c: InternalAlignment(g141,g142)
    c: InternalAlignment(g143,g142)
    c: InternalAlignment(g144,g142)
    c: Weight(g145) = 1
    c: Equal(g145,g146)
    c: Equal(g145,g147)
    c: InternalAlignment(g145,g148)
    c: InternalAlignment(g146,g148)
    c: InternalAlignment(g147,g148)
    c: InternalAlignment(g149,g148)
    c: InternalAlignment(g150,g148)
    c: Weight(g151) = 1
    c: Equal(g151,g152)
    c: Equal(g151,g153)
    c: InternalAlignment(g151,g154)
    c: InternalAlignment(g152,g154)
    c: InternalAlignment(g153,g154)
    c: InternalAlignment(g155,g154)
    c: InternalAlignment(g156,g154)
    c: Weight(g157) = 1
    c: Equal(g157,g158)
    c: Equal(g157,g159)
    c: InternalAlignment(g157,g160)
    c: InternalAlignment(g158,g160)
    c: InternalAlignment(g159,g160)
    c: InternalAlignment(g161,g160)
    c: InternalAlignment(g162,g160)
    c: Block(g160)
    c: Block(g154)
    c: Block(g148)
    c: Block(g142)
    c: Coincident(g163,g37)
    c: Coincident(g163,g160)
    c: Coincident(g164,g160)
    c: Coincident(g164,g154)
    c: Horizontal(g164)
    c: Coincident(g165,g154)
    c: Coincident(g165,g37)
    c: Vertical(g165)
    c: Coincident(g166,g31)
    c: Coincident(g166,g148)
    c: Vertical(g166)
    c: Coincident(g167,g148)
    c: Coincident(g167,g142)
    c: Horizontal(g167)
    c: Coincident(g168,g142)
    c: Coincident(g168,g31)
    c: Weight(g169) = 1
    c: Equal(g169,g170)
    c: Equal(g169,g171)
    c: InternalAlignment(g169,g172)
    c: InternalAlignment(g170,g172)
    c: InternalAlignment(g171,g172)
    c: InternalAlignment(g173,g172)
    c: InternalAlignment(g174,g172)
    c: Weight(g175) = 1
    c: Equal(g175,g176)
    c: Equal(g175,g177)
    c: InternalAlignment(g175,g178)
    c: InternalAlignment(g176,g178)
    c: InternalAlignment(g177,g178)
    c: InternalAlignment(g179,g178)
    c: InternalAlignment(g180,g178)
    c: Weight(g181) = 1
    c: Equal(g181,g182)
    c: Equal(g181,g183)
    c: InternalAlignment(g181,g184)
    c: InternalAlignment(g182,g184)
    c: InternalAlignment(g183,g184)
    c: InternalAlignment(g185,g184)
    c: InternalAlignment(g186,g184)
    c: Weight(g187) = 1
    c: Equal(g187,g188)
    c: Equal(g187,g189)
    c: InternalAlignment(g187,g190)
    c: InternalAlignment(g188,g190)
    c: InternalAlignment(g189,g190)
    c: InternalAlignment(g191,g190)
    c: InternalAlignment(g192,g190)
    c: Block(g190)
    c: Block(g184)
    c: Block(g178)
    c: Block(g172)
    c: Coincident(g193,g190)
    c: Coincident(g193,g184)
    c: Horizontal(g193)
    c: Coincident(g194,g184)
    c: Coincident(g194,g19)
    c: Vertical(g194)
    c: Coincident(g195,g25)
    c: Coincident(g195,g178)
    c: Vertical(g195)
    c: Coincident(g196,g178)
    c: Coincident(g196,g172)
    c: Horizontal(g196)
    c: Coincident(g197,g172)
    c: Coincident(g197,g25)
    c: Coincident(g198,g19)
    c: Weight(g199) = 1
    c: Equal(g199,g200)
    c: Equal(g199,g201)
    c: InternalAlignment(g199,g202)
    c: InternalAlignment(g200,g202)
    c: InternalAlignment(g201,g202)
    c: InternalAlignment(g203,g202)
    c: InternalAlignment(g204,g202)
    c: Weight(g205) = 1
    c: Equal(g205,g206)
    c: Equal(g205,g207)
    c: InternalAlignment(g205,g208)
    c: InternalAlignment(g206,g208)
    c: InternalAlignment(g207,g208)
    c: InternalAlignment(g209,g208)
    c: InternalAlignment(g210,g208)
    c: Block(g208)
    c: Block(g202)
    c: Coincident(g211,g208)
    c: Coincident(g211,g43)
    c: Coincident(g212,g43)
    c: Coincident(g212,g202)
    c: Coincident(g213,g202)
    c: Coincident(g213,g208)
    c: Vertical(g213)
    c: Weight(g214) = 1
    c: Equal(g214,g215)
    c: Equal(g214,g216)
    c: InternalAlignment(g214,g217)
    c: InternalAlignment(g215,g217)
    c: InternalAlignment(g216,g217)
    c: InternalAlignment(g218,g217)
    c: InternalAlignment(g219,g217)
    c: Weight(g220) = 1
    c: Equal(g220,g221)
    c: Equal(g220,g222)
    c: InternalAlignment(g220,g223)
    c: InternalAlignment(g221,g223)
    c: InternalAlignment(g222,g223)
    c: InternalAlignment(g224,g223)
    c: InternalAlignment(g225,g223)
    c: Block(g223)
    c: Block(g217)
    c: Coincident(g226,g217)
    c: Coincident(g226,g49)
    c: Coincident(g227,g49)
    c: Coincident(g227,g223)
    c: Coincident(g228,g223)
    c: Coincident(g228,g217)
    c: Vertical(g228)
    c: Horizontal(g229)
    c: Block(g229)
    c: Vertical(g230)
    c: Block(g230)
    c: Block(g231)
    c: Weight(g232) = 1
    c: Equal(g232,g233)
    c: Equal(g232,g234)
    c: InternalAlignment(g232,g235)
    c: InternalAlignment(g233,g235)
    c: InternalAlignment(g234,g235)
    c: InternalAlignment(g236,g235)
    c: InternalAlignment(g237,g235)
    c: Weight(g238) = 1
    c: Equal(g238,g239)
    c: Equal(g238,g240)
    c: InternalAlignment(g238,g241)
    c: InternalAlignment(g239,g241)
    c: InternalAlignment(g240,g241)
    c: InternalAlignment(g242,g241)
    c: InternalAlignment(g243,g241)
    c: Weight(g244) = 1
    c: Equal(g244,g245)
    c: Equal(g244,g246)
    c: InternalAlignment(g244,g247)
    c: InternalAlignment(g245,g247)
    c: InternalAlignment(g246,g247)
    c: InternalAlignment(g248,g247)
    c: InternalAlignment(g249,g247)
    c: Weight(g250) = 1
    c: Equal(g250,g251)
    c: Equal(g250,g252)
    c: InternalAlignment(g250,g253)
    c: InternalAlignment(g251,g253)
    c: InternalAlignment(g252,g253)
    c: InternalAlignment(g254,g253)
    c: InternalAlignment(g255,g253)
    c: Block(g235)
    c: Block(g241)
    c: Block(g247)
    c: Block(g253)
    c: Coincident(g256,g241)
    c: Coincident(g256,g235)
    c: Horizontal(g256)
    c: Block(g198)
    c: Weight(g257) = 1
    c: Equal(g257,g258)
    c: Equal(g257,g259)
    c: InternalAlignment(g257,g260)
    c: InternalAlignment(g258,g260)
    c: InternalAlignment(g259,g260)
    c: InternalAlignment(g261,g260)
    c: InternalAlignment(g262,g260)
    c: Weight(g263) = 1
    c: Equal(g263,g264)
    c: Equal(g263,g265)
    c: InternalAlignment(g263,g266)
    c: InternalAlignment(g264,g266)
    c: InternalAlignment(g265,g266)
    c: InternalAlignment(g267,g266)
    c: InternalAlignment(g268,g266)
    c: Weight(g269) = 1
    c: Equal(g269,g270)
    c: Equal(g269,g271)
    c: InternalAlignment(g269,g272)
    c: InternalAlignment(g270,g272)
    c: InternalAlignment(g271,g272)
    c: InternalAlignment(g273,g272)
    c: InternalAlignment(g274,g272)
    c: Weight(g275) = 1
    c: Equal(g275,g276)
    c: Equal(g275,g277)
    c: InternalAlignment(g275,g278)
    c: InternalAlignment(g276,g278)
    c: InternalAlignment(g277,g278)
    c: InternalAlignment(g279,g278)
    c: InternalAlignment(g280,g278)
    c: Block(g260)
    c: Block(g266)
    c: Block(g272)
    c: Block(g278)
    c: Coincident(g281,g272)
    c: Coincident(g281,g278)
    c: Horizontal(g281)
    c: Coincident(g282,g278)
    c: Coincident(g282,g260)
    c: Vertical(g282)
    c: Coincident(g283,g260)
    c: Coincident(g283,g266)
    c: Coincident(g284,g266)
    c: Coincident(g284,g272)
    c: Vertical(g284)
    c: Weight(g285) = 1
    c: Equal(g285,g286)
    c: Equal(g285,g287)
    c: InternalAlignment(g285,g288)
    c: InternalAlignment(g286,g288)
    c: InternalAlignment(g287,g288)
    c: InternalAlignment(g289,g288)
    c: InternalAlignment(g290,g288)
    c: Weight(g291) = 1
    c: Equal(g291,g292)
    c: Equal(g291,g293)
    c: InternalAlignment(g291,g294)
    c: InternalAlignment(g292,g294)
    c: InternalAlignment(g293,g294)
    c: InternalAlignment(g295,g294)
    c: InternalAlignment(g296,g294)
    c: Weight(g297) = 1
    c: Equal(g297,g298)
    c: Equal(g297,g299)
    c: InternalAlignment(g297,g300)
    c: InternalAlignment(g298,g300)
    c: InternalAlignment(g299,g300)
    c: InternalAlignment(g301,g300)
    c: InternalAlignment(g302,g300)
    c: Block(g300)
    c: Block(g294)
    c: Block(g288)
    c: Coincident(g303,g294)
    c: Coincident(g303,g288)
    c: Coincident(g304,g288)
    c: Coincident(g304,g300)
    c: Vertical(g304)
    c: Coincident(g305,g300)
    c: Coincident(g305,g294)
    c: Horizontal(g305)
    c: Weight(g306) = 1
    c: Equal(g306,g307)
    c: InternalAlignment(g306,g308)
    c: InternalAlignment(g307,g308)
    c: InternalAlignment(g309,g308)
    c: InternalAlignment(g310,g308)
    c: Weight(g311) = 1
    c: Equal(g311,g312)
    c: Equal(g311,g313)
    c: InternalAlignment(g311,g314)
    c: InternalAlignment(g312,g314)
    c: InternalAlignment(g313,g314)
    c: InternalAlignment(g315,g314)
    c: InternalAlignment(g316,g314)
    c: Weight(g317) = 1
    c: Equal(g317,g318)
    c: Equal(g317,g319)
    c: InternalAlignment(g317,g320)
    c: InternalAlignment(g318,g320)
    c: InternalAlignment(g319,g320)
    c: InternalAlignment(g321,g320)
    c: InternalAlignment(g322,g320)
    c: Equal(g323,g324)
    c: Equal(g323,g325)
    c: InternalAlignment(g323,g326)
    c: InternalAlignment(g324,g326)
    c: InternalAlignment(g325,g326)
    c: InternalAlignment(g327,g326)
    c: InternalAlignment(g328,g326)
    c: Block(g314)
    c: Block(g320)
    c: Block(g326)
    c: Block(g308)
    c: Coincident(g329,g308)
    c: Coincident(g329,g314)
    c: Horizontal(g329)
    c: Coincident(g330,g314)
    c: Coincident(g330,g320)
    c: Vertical(g330)
    c: Coincident(g331,g320)
    c: Coincident(g331,g326)
    c: Horizontal(g331)
    c: Coincident(g332,g326)
    c: Coincident(g332,g308)
FEATURE [Sketcher::SketchObject] Sketch001
  FullyConstrained = true
  MapMode = 4
  Placement = pos=(0,0,0) rot=(0.57735,0.57735,0.57735;2.0944rad)
  Support = -> [Sketch]
  sketch-geometry (46):
    g0: BSplineCurve PolesCount=3 KnotsCount=2 Degree=2 IsPeriodic=0
    g1: ArcOfCircle CenterX=73.1223 CenterY=-32.291 CenterZ=0 NormalX=0 NormalY=0 NormalZ=1 AngleXU=0 Radius=13 StartAngle=5.92268 EndAngle=9.06428
    g2: ArcOfCircle CenterX=66.7816 CenterY=-49.1439 CenterZ=0 NormalX=0 NormalY=0 NormalZ=1 AngleXU=0 Radius=13 StartAngle=2.78068 EndAngle=5.92131
    g3: ArcOfCircle CenterX=55.9263 CenterY=-78.1807 CenterZ=0 NormalX=0 NormalY=0 NormalZ=1 AngleXU=0 Radius=13 StartAngle=5.92268 EndAngle=9.06428
    g4: ArcOfCircle CenterX=49.5884 CenterY=-95.0342 CenterZ=0 NormalX=0 NormalY=0 NormalZ=1 AngleXU=0 Radius=13 StartAngle=2.78068 EndAngle=5.92131
    g5: ArcOfCircle CenterX=38.7206 CenterY=-124.067 CenterZ=0 NormalX=0 NormalY=0 NormalZ=1 AngleXU=0 Radius=13 StartAngle=5.92268 EndAngle=9.06428
    g6: ArcOfCircle CenterX=32.3875 CenterY=-140.92 CenterZ=0 NormalX=0 NormalY=0 NormalZ=1 AngleXU=0 Radius=13 StartAngle=2.78068 EndAngle=5.92131
    g7: ArcOfCircle CenterX=21.4715 CenterY=-169.934 CenterZ=0 NormalX=0 NormalY=0 NormalZ=1 AngleXU=0 Radius=13 StartAngle=5.92268 EndAngle=9.06428
    g8: ArcOfCircle CenterX=15.1336 CenterY=-186.787 CenterZ=0 NormalX=0 NormalY=0 NormalZ=1 AngleXU=0 Radius=13 StartAngle=2.78068 EndAngle=5.92131
    g9-g12: Circle x4 (B-spline internal-alignment scaffolding for g13; pole/knot coordinates omitted)
    g13: BSplineCurve PolesCount=4 KnotsCount=2 Degree=3 IsPeriodic=0
    g14: GeomPoint X=28.8094 Y=-19.0875 Z=0
    g15: GeomPoint X=47.0443 Y=-50.4712 Z=0
    g16: Circle CenterX=53.5586 CenterY=-23.2695 CenterZ=0 NormalX=0 NormalY=0 NormalZ=1 AngleXU=0 Radius=3.24518
    g17: Circle CenterX=-195.441 CenterY=-127.082 CenterZ=0 NormalX=0 NormalY=0 NormalZ=1 AngleXU=0 Radius=1
    g18: Circle CenterX=-8.24091 CenterY=-197.481 CenterZ=0 NormalX=0 NormalY=0 NormalZ=1 AngleXU=0 Radius=1
    g19: Circle CenterX=12.8789 CenterY=-141.321 CenterZ=0 NormalX=0 NormalY=0 NormalZ=1 AngleXU=0 Radius=1
    g20: BSplineCurve PolesCount=3 KnotsCount=2 Degree=2 IsPeriodic=0
    g21: GeomPoint X=-195.441 Y=-127.082 Z=0
    g22: GeomPoint X=12.8789 Y=-141.321 Z=0
    g23: Circle CenterX=-12.8016 CenterY=-179.036 CenterZ=0 NormalX=0 NormalY=0 NormalZ=1 AngleXU=0 Radius=10.5072
    g24: Circle CenterX=0.933922 CenterY=-166.43 CenterZ=0 NormalX=0 NormalY=0 NormalZ=1 AngleXU=0 Radius=3.26661
    g25: Circle CenterX=-33.5518 CenterY=-176.44 CenterZ=0 NormalX=0 NormalY=0 NormalZ=1 AngleXU=0 Radius=5.64388
    g26: Circle CenterX=-47.2366 CenterY=-173.859 CenterZ=0 NormalX=0 NormalY=0 NormalZ=1 AngleXU=0 Radius=3.01653
    g27: Circle CenterX=-56.2595 CenterY=-171.456 CenterZ=0 NormalX=0 NormalY=0 NormalZ=1 AngleXU=0 Radius=2.12826
    g28: ArcOfCircle CenterX=51.2151 CenterY=-198.473 CenterZ=0 NormalX=0 NormalY=0 NormalZ=1 AngleXU=0 Radius=20 StartAngle=2.78189 EndAngle=4.35269
    g29: LineSegment StartX=32.4951 StartY=-191.433 StartZ=0 EndX=94.6578 EndY=-26.1352 EndZ=0
    g30: LineSegment StartX=43.1192 StartY=-220.001 StartZ=0 EndX=-196.497 EndY=-129.89 EndZ=0
    g31: LineSegment StartX=43.1192 StartY=-220.001 StartZ=0 EndX=44.1752 EndY=-217.193 EndZ=0
    g32: LineSegment StartX=117.223 StartY=-19.0875 StartZ=0 EndX=117.223 EndY=-16.0875 EndZ=0
    g33: LineSegment StartX=117.223 StartY=-16.0875 StartZ=0 EndX=17.2232 EndY=-16.0875 EndZ=0
    g34: LineSegment StartX=17.2232 StartY=-16.0875 StartZ=0 EndX=17.2232 EndY=-19.0875 EndZ=0
    g35: LineSegment StartX=28.8094 StartY=-19.0875 StartZ=0 EndX=17.2232 EndY=-19.0875 EndZ=0
    g36: LineSegment StartX=47.0443 StartY=-50.4712 StartZ=0 EndX=12.8789 EndY=-141.321 EndZ=0
    g37: LineSegment StartX=-195.441 StartY=-127.082 StartZ=0 EndX=-196.497 EndY=-129.89 EndZ=0
    g38: LineSegment StartX=85.2866 StartY=-36.8766 StartZ=0 EndX=78.9396 EndY=-53.7463 EndZ=0
    g39: LineSegment StartX=60.9579 StartY=-27.7053 StartZ=0 EndX=54.6191 EndY=-44.5532 EndZ=0
    g40: LineSegment StartX=68.0907 StartY=-82.7664 StartZ=0 EndX=61.7465 EndY=-99.6365 EndZ=0
    g41: LineSegment StartX=43.7619 StartY=-73.595 StartZ=0 EndX=37.426 EndY=-90.4435 EndZ=0
    g42: LineSegment StartX=50.885 StartY=-128.652 StartZ=0 EndX=44.5456 EndY=-145.522 EndZ=0
    g43: LineSegment StartX=26.5562 StartY=-119.481 StartZ=0 EndX=20.2251 EndY=-136.329 EndZ=0
    g44: LineSegment StartX=9.3071 StartY=-165.349 StartZ=0 EndX=2.97115 EndY=-182.197 EndZ=0
    g45: LineSegment StartX=33.6358 StartY=-174.52 StartZ=0 EndX=27.2917 EndY=-191.39 EndZ=0
  constraints (71):
    c: Block(g0)
    c: Block(g1)
    c: Block(g2)
    c: Block(g4)
    c: Block(g3)
    c: Block(g6)
    c: Block(g5)
    c: Block(g8)
    c: Block(g7)
    c: Weight(g9) = 1
    c: Equal(g9,g10)
    c: Equal(g9,g11)
    c: Equal(g9,g12)
    c: InternalAlignment(g9-g12 -> g13) x4
    c: InternalAlignment(g14,g13)
    c: InternalAlignment(g15,g13)
    c: Block(g16)
    c: Weight(g17) = 1
    c: Equal(g17,g18)
    c: Equal(g17,g19)
    c: InternalAlignment(g17,g20)
    c: InternalAlignment(g18,g20)
    c: InternalAlignment(g19,g20)
    c: InternalAlignment(g21,g20)
    c: InternalAlignment(g22,g20)
    c: Block(g20)
    c: Block(g23)
    c: Block(g24)
    c: Block(g25)
    c: Block(g26)
    c: Block(g27)
    c: Block(g28)
    c: Coincident(g29,g28)
    c: Coincident(g29,g0)
    c: Block(g13)
    c: Coincident(g31,g30)
    c: Coincident(g31,g28)
    c: Block(g31)
    c: Coincident(g32,g0)
    c: Vertical(g32)
    c: Coincident(g33,g32)
    c: Horizontal(g33)
    c: Coincident(g34,g33)
    c: Vertical(g34)
    c: Block(g33)
    c: Coincident(g35,g13)
    c: Coincident(g35,g34)
    c: Horizontal(g35)
    c: Coincident(g36,g13)
    c: Coincident(g36,g20)
    c: Coincident(g37,g20)
    c: Coincident(g37,g30)
    c: Block(g30)
    c: Coincident(g38,g1)
    c: Coincident(g38,g2)
    c: Coincident(g39,g1)
    c: Coincident(g39,g2)
    c: Coincident(g40,g3)
    c: Coincident(g40,g4)
    c: Coincident(g41,g3)
    c: Coincident(g41,g4)
    c: Coincident(g42,g5)
    c: Coincident(g42,g6)
    c: Coincident(g43,g5)
    c: Coincident(g43,g6)
    c: Coincident(g44,g7)
    c: Coincident(g44,g8)
    c: Coincident(g45,g7)
    c: Coincident(g45,g8)
    c: Distance(g30) = 256
    c: Distance(g33) = 100
FEATURE [Part::Extrusion] Extrude002
  Base = -> Sketch001
  Dir = (1,0,0)
  DirMode = 2
  FaceMakerClass = Part::FaceMakerBullseye
  LengthFwd = 8
  LengthRev = 0
  Solid = true
  Symmetric = false
FEATURE [Sketcher::SketchObject] Sketch002
  FullyConstrained = true
  sketch-geometry (20):
    g0: LineSegment StartX=-2.77179 StartY=-200.304 StartZ=0 EndX=5.22821 EndY=-200.304 EndZ=0
    g1: LineSegment StartX=5.22821 StartY=-200.304 StartZ=0 EndX=5.22821 EndY=-197.304 EndZ=0
    g2: LineSegment StartX=-2.77179 StartY=-200.304 StartZ=0 EndX=-2.77179 EndY=-197.304 EndZ=0
    g3: LineSegment StartX=5.22821 StartY=-197.304 StartZ=0 EndX=8.22821 EndY=-197.304 EndZ=0
    g4: LineSegment StartX=-2.77179 StartY=-197.304 StartZ=0 EndX=-5.77179 EndY=-197.304 EndZ=0
    g5: LineSegment StartX=19.2282 StartY=-203.304 StartZ=0 EndX=19.2282 EndY=-206.304 EndZ=0
    g6: LineSegment StartX=-16.7718 StartY=-203.304 StartZ=0 EndX=-16.7718 EndY=-206.304 EndZ=0
    g7: LineSegment StartX=-16.7718 StartY=-206.304 StartZ=0 EndX=19.2282 EndY=-206.304 EndZ=0
    g8: Circle CenterX=-16.7718 CenterY=-203.304 CenterZ=0 NormalX=0 NormalY=0 NormalZ=1 AngleXU=0 Radius=1
    g9: Circle CenterX=-5.77179 CenterY=-203.304 CenterZ=0 NormalX=0 NormalY=0 NormalZ=1 AngleXU=0 Radius=1
    g10: Circle CenterX=-5.77179 CenterY=-197.304 CenterZ=0 NormalX=0 NormalY=0 NormalZ=1 AngleXU=0 Radius=1
    g11: BSplineCurve PolesCount=3 KnotsCount=2 Degree=2 IsPeriodic=0
    g12: GeomPoint X=-16.7718 Y=-203.304 Z=0
    g13: GeomPoint X=-5.77179 Y=-197.304 Z=0
    g14: Circle CenterX=19.2282 CenterY=-203.304 CenterZ=0 NormalX=0 NormalY=0 NormalZ=1 AngleXU=0 Radius=1
    g15: Circle CenterX=8.22821 CenterY=-203.304 CenterZ=0 NormalX=0 NormalY=0 NormalZ=1 AngleXU=0 Radius=1
    g16: Circle CenterX=8.22821 CenterY=-197.304 CenterZ=0 NormalX=0 NormalY=0 NormalZ=1 AngleXU=0 Radius=1
    g17: BSplineCurve PolesCount=3 KnotsCount=2 Degree=2 IsPeriodic=0
    g18: GeomPoint X=19.2282 Y=-203.304 Z=0
    g19: GeomPoint X=8.22821 Y=-197.304 Z=0
  constraints (41):
    c: Horizontal(g0)
    c: Distance(g0) = 8
    c: Coincident(g1,g0)
    c: Vertical(g1)
    c: Distance(g1) = 3
    c: Coincident(g2,g0)
    c: Vertical(g2)
    c: Distance(g2) = 3
    c: Coincident(g3,g1)
    c: Horizontal(g3)
    c: Distance(g3) = 3
    c: Coincident(g4,g2)
    c: Horizontal(g4)
    c: Distance(g4) = 3
    c: Vertical(g5)
    c: Vertical(g6)
    c: Coincident(g7,g6)
    c: Coincident(g7,g5)
    c: Weight(g8) = 1
    c: Equal(g8,g9)
    c: Equal(g8,g10)
    c: Coincident(g11,g4)
    c: InternalAlignment(g8,g11)
    c: InternalAlignment(g9,g11)
    c: InternalAlignment(g10,g11)
    c: InternalAlignment(g12,g11)
    c: InternalAlignment(g13,g11)
    c: Coincident(g17,g5)
    c: Weight(g14) = 1
    c: Equal(g14,g15)
    c: Equal(g14,g16)
    c: Coincident(g17,g3)
    c: InternalAlignment(g14,g17)
    c: InternalAlignment(g15,g17)
    c: InternalAlignment(g16,g17)
    c: InternalAlignment(g18,g17)
    c: InternalAlignment(g19,g17)
    c: Block(g7)
    c: Block(g17)
    c: Block(g11)
    c: Block(g6)
FEATURE [Part::Extrusion] Extrude003
  Base = -> Sketch002
  Dir = (0,0,1)
  DirMode = 2
  FaceMakerClass = Part::FaceMakerBullseye
  LengthFwd = 260
  LengthRev = 0
  Solid = true
  Symmetric = false
FEATURE [Part::Extrusion] Extrude
  Base = -> Sketch
  Dir = (0,0,1)
  DirMode = 2
  FaceMakerClass = Part::FaceMakerBullseye
  LengthFwd = 14
  LengthRev = 0
  Solid = true
  Symmetric = false
